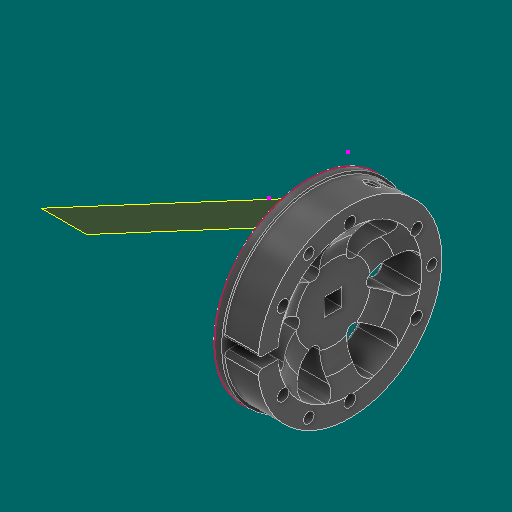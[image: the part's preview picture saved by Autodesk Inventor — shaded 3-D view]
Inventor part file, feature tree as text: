
AUTODESK INVENTOR PART (.ipt)
format: ipt  version: 2023.1 (Build 271208000, 208)  size: 559,104 bytes
history: native  units: in
note: dims shown in document units (in); Inventor stores cm internally (conversion verified against a paired STEP export)
features: sketch x7, other x4, plane x1
ambient origin geometry x8: Origin, YZ Plane, XZ Plane, XY Plane, X Axis, Y Axis, Z Axis, Center Point
bodies: Solid1 (feature_tree)
feature tree (12):
  other  "WheelHalf_MIR1.ipt"
  other  "Solid1::WheelHalf_MIR1.ipt"
  other  "TaggingFeature1"
  sketch  "Sketch1"  dims[d0=0.3937in]
  sketch  "Sketch2"
  sketch  "Sketch3"
  sketch  "Sketch4"
  sketch  "Sketch5"
  sketch  "Sketch6"
  sketch  "Sketch7"
  plane  "Work Plane1"
  other  "Work Axis1"
